# Revit family: Rohrschelle Maxima PSM, M16, Ø120-275, Silikon
name_source: partatom
category: HLS-Bauteile
revit_build: Autodesk Revit 2017 (Build: 20190507_1515(x64)
units: mm (PartAtom-declared; Revit-internal decimal feet)

## family parameters
Arbeitsebenenbasiert = Ja
Beim Laden mit Abzugskörper schneiden = Nein
Bemaßung runder Anschluss = Durchmesser verwenden
Gemeinsam genutzt = Ja
Immer vertikal = Nein
Raumberechnungspunkt = Nein
Teiletyp = Normal

## types (15) — shared parameters
A = 30 mm  [stored 0.0984252 ft]
Anschluss = M16
Anschlußhöhe = 30 mm
Bauart = zweiteilig
Baustoffklasse = B2
Brandschutz = 901-1118-000-La-Pk
DF1 = 30 mm  [stored 0.0984252 ft]
DF2 = 34 mm
DS = 6 mm  [stored 0.019685 ft]
DVS = 18 mm  [stored 0.0590551 ft]
Dämmstärke = 6 mm  [stored 0.019685 ft]
Fabrikat = MEFA
Farbe Schalldämmeinlage = rot
Firma = MEFA Befestigungs- und Montagesysteme GmbH
HGA = 20 mm  [stored 0.0656168 ft]
Kurztext1 = Rohrschelle Maxima PSM 35x4,0
MB = 35 mm  [stored 0.114829 ft]
MD = 4 mm  [stored 0.0131234 ft]
Material = Stahl
Material Schalldämmeinlage = Silikon
Materialmaße = 35x4,0 mm
Materialname = S235
Mengeneinheit = St
Oberflaeche = galvanisch verzinkt
Schalldämmeinlage = Silikon
Verschluss = Pendelsteckmuttern
Verschluss-Schraube = M10
Vorgabe-Ansicht = 1219 mm
max. Temperaturbeständigkeit = 250 °C
max. zul. Last = 5.00 kN
max. zul. Last horizontal = 0.00 kN
max. zul. Last vertikal = 0.00 kN
vpe = 1 St
zero-valued in all types: Nennweite DN Rohr, Rohraußendurchmesser, Stärke Material

## per-type parameters (varying)
| type | AB | Achsabstand | Artikelnummer | B | Breite | D | D0 | Dmax | Dmin | EAN | Gewicht | Gewicht pro Bauteil | H | Kurztext2 | R | RM | Rohraußendurchmesser Zoll | S | max. Höhe | max. Rohraußendurchmesser | min. Rohraußendurchmesser |
| Maxima PSM, M16, Ø120-125, Silikon | 5 mm  [stored 0.0164042 ft] | 179 mm | 0084665 | 209 mm | 209 mm | 125 mm  [stored 0.410105 ft] | 137 mm | 125 mm  [stored 0.410105 ft] | 120 mm  [stored 0.393701 ft] | 4250928406934 | 0.83 kg | 0.83 kg | 165 mm | 120 - 125 mm M16 Silikon | 69 mm | 73 mm | Zoll | 179 mm | 165 mm | 125 mm  [stored 0.410105 ft] | 120 mm  [stored 0.393701 ft] |
| Maxima PSM, M16, Ø127-132, Silikon | 5 mm  [stored 0.0164042 ft] | 186 mm | 0084670 | 216 mm | 216 mm | 132 mm  [stored 0.433071 ft] | 144 mm | 132 mm  [stored 0.433071 ft] | 127 mm | 4250928406941 | 0.86 kg | 0.86 kg | 172 mm | 127 - 132 mm M16 Silikon | 72 mm  [stored 0.23622 ft] | 76 mm  [stored 0.249344 ft] | Zoll | 186 mm | 172 mm | 132 mm  [stored 0.433071 ft] | 127 mm |
| Maxima PSM, M16, Ø133-136, Silikon | 3 mm  [stored 0.00984252 ft] | 190 mm | 0084689 | 220 mm | 220 mm | 136 mm | 148 mm | 136 mm | 133 mm  [stored 0.436352 ft] | 4250928406958 | 0.88 kg | 0.88 kg | 176 mm | 133 - 136 mm M16 Silikon | 74 mm  [stored 0.242782 ft] | 78 mm  [stored 0.255906 ft] | Zoll | 190 mm | 176 mm | 136 mm | 133 mm  [stored 0.436352 ft] |
| Maxima PSM, M16, Ø137-142, Silikon | 5 mm  [stored 0.0164042 ft] | 196 mm | 0084692 | 226 mm | 226 mm | 142 mm | 154 mm | 142 mm | 137 mm | 4250928406965 | 0.90 kg | 0.90 kg | 182 mm | 137 - 142 mm M16 Silikon | 77 mm  [stored 0.252625 ft] | 81 mm | 5 Zoll | 196 mm | 182 mm | 142 mm | 137 mm |
| Maxima PSM, M16, Ø145-150, Silikon | 5 mm  [stored 0.0164042 ft] | 204 mm | 0084693 | 234 mm | 234 mm | 150 mm | 162 mm | 150 mm | 145 mm | 4250928406972 | 0.94 kg | 0.94 kg | 190 mm | 145 - 150 mm M16 Silikon | 81 mm | 85 mm | Zoll | 204 mm | 190 mm | 150 mm | 145 mm |
| Maxima PSM, M16, Ø152-156, Silikon | 4 mm  [stored 0.0131234 ft] | 210 mm | 0084703 | 240 mm | 240 mm | 156 mm | 168 mm | 156 mm | 152 mm | 4250928406989 | 0.97 kg | 0.97 kg | 196 mm | 152 - 156 mm M16 Silikon | 84 mm  [stored 0.275591 ft] | 88 mm | Zoll | 210 mm | 196 mm | 156 mm | 152 mm |
| Maxima PSM, M16, Ø158-163, Silikon | 5 mm  [stored 0.0164042 ft] | 217 mm | 0084719 | 247 mm | 247 mm | 163 mm | 175 mm | 163 mm | 158 mm | 4250928406996 | 1.00 kg | 1.00 kg | 203 mm | 158 - 163 mm M16 Silikon | 88 mm | 92 mm | Zoll | 217 mm | 203 mm | 163 mm | 158 mm |
| Maxima PSM, M16, Ø164-168, Silikon | 4 mm  [stored 0.0131234 ft] | 222 mm | 0084723 | 252 mm | 252 mm | 168 mm | 180 mm | 168 mm | 164 mm | 4250928407009 | 1.02 kg | 1.02 kg | 208 mm | 164 - 168 mm M16 Silikon | 90 mm  [stored 0.295276 ft] | 94 mm | 6 Zoll | 222 mm | 208 mm | 168 mm | 164 mm |
| Maxima PSM, M16, Ø190-194, Silikon | 4 mm  [stored 0.0131234 ft] | 248 mm | 0084750 | 278 mm | 278 mm | 194 mm | 206 mm | 194 mm | 190 mm | 4250928407016 | 1.14 kg | 1.14 kg | 234 mm | 190 - 194 mm M16 Silikon | 103 mm  [stored 0.337927 ft] | 107 mm  [stored 0.35105 ft] | Zoll | 248 mm | 234 mm | 194 mm | 190 mm |
| Maxima PSM, M16, Ø198-203, Silikon | 5 mm  [stored 0.0164042 ft] | 257 mm | 0084754 | 287 mm | 287 mm | 203 mm | 215 mm | 203 mm | 198 mm | 4250928407023 | 1.17 kg | 1.17 kg | 243 mm | 198 - 203 mm M16 Silikon | 108 mm | 112 mm | Zoll | 257 mm | 243 mm | 203 mm | 198 mm |
| Maxima PSM, M16, Ø207-213, Silikon | 6 mm  [stored 0.019685 ft] | 267 mm | 0084794 | 297 mm | 297 mm | 213 mm | 225 mm | 213 mm | 207 mm | 4250928407030 | 1.21 kg | 1.21 kg | 253 mm | 207 - 213 mm M16 Silikon | 113 mm | 117 mm | Zoll | 267 mm | 253 mm | 213 mm | 207 mm |
| Maxima PSM, M16, Ø219-223, Silikon | 4 mm  [stored 0.0131234 ft] | 277 mm | 0084811 | 307 mm | 307 mm | 223 mm | 235 mm | 223 mm | 219 mm | 4250928407047 | 1.27 kg | 1.27 kg | 263 mm | 219 - 223 mm M16 Silikon | 118 mm | 122 mm | 8 Zoll | 277 mm | 263 mm | 223 mm | 219 mm |
| Maxima PSM, M16, Ø225-230, Silikon | 5 mm  [stored 0.0164042 ft] | 284 mm | 0084816 | 314 mm | 314 mm | 230 mm | 242 mm | 230 mm | 225 mm | 4250928407054 | 1.29 kg | 1.29 kg | 270 mm | 225 - 230 mm M16 Silikon | 121 mm  [stored 0.396982 ft] | 125 mm  [stored 0.410105 ft] | Zoll | 284 mm | 270 mm | 230 mm | 225 mm |
| Maxima PSM, M16, Ø242-246, Silikon | 4 mm  [stored 0.0131234 ft] | 300 mm | 0084832 | 330 mm | 330 mm | 246 mm | 258 mm | 246 mm | 242 mm | 4250928407061 | 1.37 kg | 1.37 kg | 286 mm | 242 - 246 mm M16 Silikon | 129 mm | 133 mm  [stored 0.436352 ft] | Zoll | 300 mm | 286 mm | 246 mm | 242 mm |
| Maxima PSM, M16, Ø270-275, Silikon | 5 mm  [stored 0.0164042 ft] | 329 mm | 0084870 | 359 mm | 359 mm | 275 mm | 287 mm | 275 mm | 270 mm | 4250928407078 | 1.49 kg | 1.49 kg | 315 mm | 270 - 275 mm M16 Silikon | 144 mm | 148 mm | 10 Zoll | 329 mm | 315 mm | 275 mm | 270 mm |

note: [stored X ft] marks values corroborated as IEEE doubles in the binary element streams (Revit-internal decimal feet)

## geometry (parser evidence)
native form markers: Sweep x6
no freeform markers — native parametric forms only
